# Revit family: Power-Teknion-YMSUSA_Swerv_USB_Hub_Single_Standard_Plug_In-R2022
name_source: partatom
category: Furniture
units: mm (PartAtom-declared; Revit-internal decimal feet)

## family parameters
Always vertical = Yes
Cut with Voids When Loaded = No
Enable Cutting in Views = No
OmniClass Number = 23.40.20.00
OmniClass Title = General Furniture and Specialties
Render Appearance Source = Family Geometry
Room Calculation Point = No
Shared = Yes
Work Plane-Based = No

## types (8) — shared parameters
Assembly Code = E2020200
Manufacturer = Teknion
Manufacturer Fax = 416.661.4586
Part Number = YMSUSA
Product Documentation Link = https://www.teknion.com
Product Line = Accessories
Product Page URL = https://www.teknion.com
Series = Complements
Sustainability Data = https://www.teknion.com
URL = www.teknion.com
Unit Weight URL = http://www.teknion.com
Warranty = http://www.teknion.com
zero-valued in all types: Default Elevation, Depth, Length, Width

## per-type parameters (varying)
| type | AA Configuration | AC Configuration | Deep Knife Cover Undermount | Description | Edge Clamp | Height | Magnetic Under Shelf Mount | Model | Non-Cover Undermount | Standard Cover Undermount | Thickness | Type C Hole | USB Hole |
| AA Configuration with Edge Clamp | Yes | No | No | Swerv USB Hub Single, Standard Plug-In, AA Configuration with Edge Clamp | Yes | 29.984 " | No | YMSUSAAAENN | No | No | 0.984 " | 0.2 " | 0.384 " |
| AA Configuration with Magnetic Under Shelf Mount | Yes | No | No | Swerv USB Hub Single, Standard Plug-In, AA Configuration with Magnetic Under Shelf Mount | No | 29.984 " | Yes | YMSUSAAAMNN | No | No | 0.984 " | 0.2 " | 0.384 " |
| AA Configuration with Non-Cover Undermount | Yes | No | No | Swerv USB Hub Single, Standard Plug-In, AA Configuration with Non-Cover Undermount | No | 29.984 " | No | YMSUSAAAUNN | Yes | No | 0.984 " | 0.2 " | 0.384 " |
| AC Configuration with Non-Cover Undermount | No | Yes | No | Swerv USB Hub Single, Standard Plug-In, AC Configuration with Non-Cover Undermount | No | 29.602 " | No | YMSUSAACUNN | Yes | No | 0.602 " | 0.042 " | 0.2 " |
| AC Configuration with Edge Clamp | No | Yes | No | Swerv USB Hub Single, Standard Plug-In, AC Configuration with Edge Clamp | Yes | 29.602 " | No | YMSUSAACENN | No | No | 0.602 " | 0.042 " | 0.2 " |
| AC Configuration with Magnetic Under Shelf Mount | No | Yes | No | Swerv USB Hub Single, Standard Plug-In, AC Configuration with Magnetic Under Shelf Mount | No | 29.602 " | Yes | YMSUSAACMNN | No | No | 0.602 " | 0.042 " | 0.2 " |
| AC Configuration with Undermount Deep Knife Cover | No | Yes | Yes | Swerv USB Hub Single, Standard Plug-In, AC Configuration with Undermount Deep Knife Cover | No | 29.602 " | No | YMSUSAACUDK | No | No | 0.602 " | 0.042 " | 0.2 " |
| AC Configuration with Undermount Standard Cover | No | Yes | No | Swerv USB Hub Single, Standard Plug-In, AC Configuration with Undermount Standard Cover | No | 29.602 " | No | YMSUSAACUSC | No | Yes | 0.602 " | 0.042 " | 0.2 " |

## geometry (parser evidence)
native form markers: Sweep x17
no freeform markers — native parametric forms only
